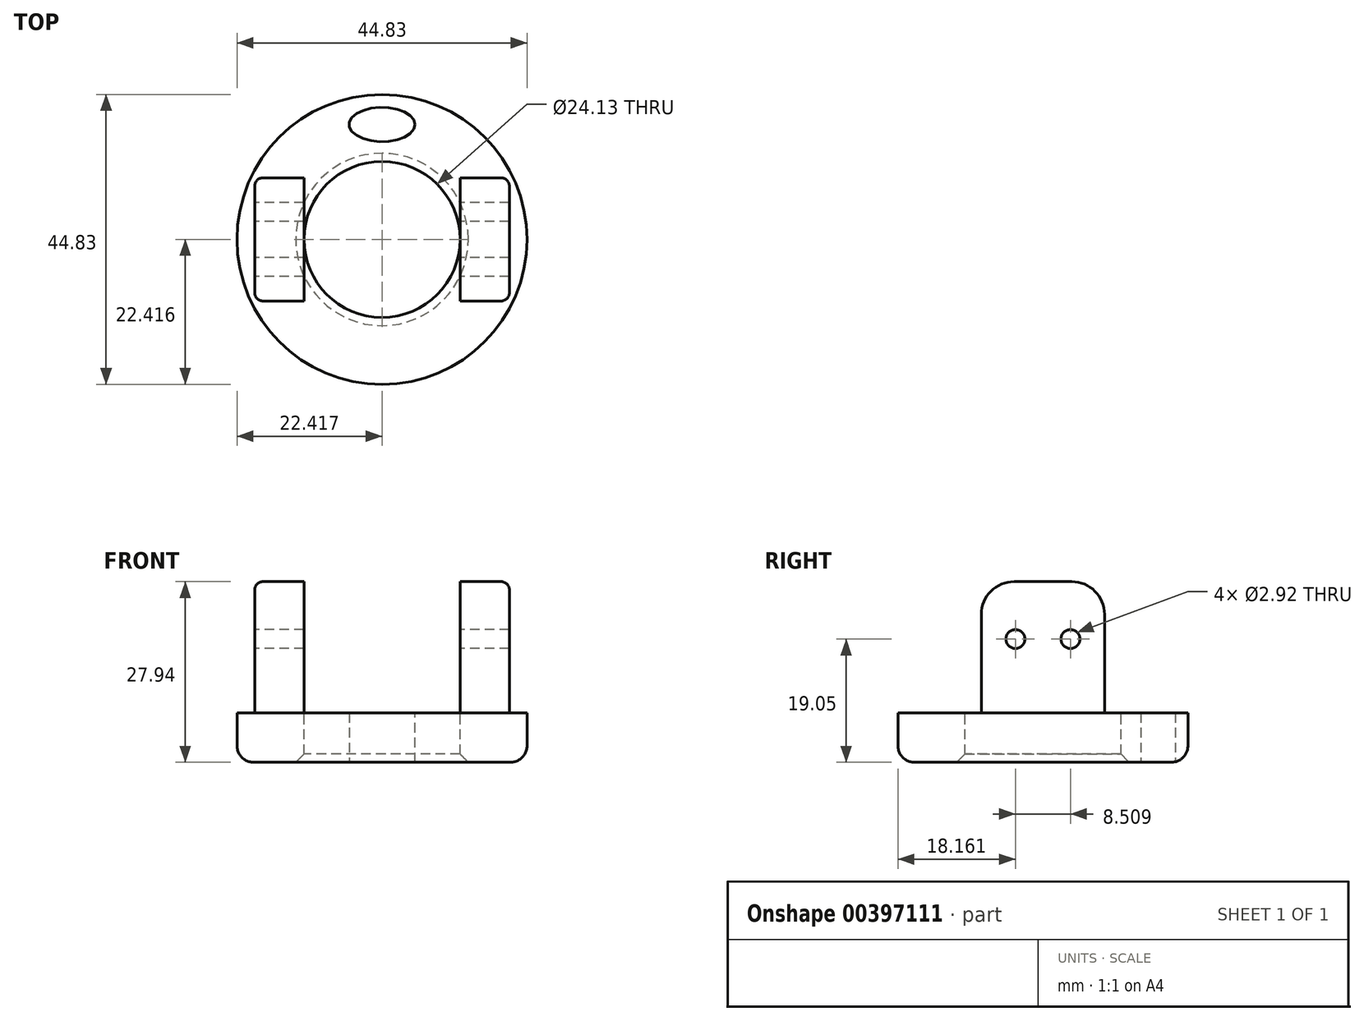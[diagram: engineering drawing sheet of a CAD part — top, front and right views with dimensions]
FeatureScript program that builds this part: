
annotation { "Feature Type Name" : "Feature", "Feature Type Description" : "" }
export const myFeature = defineFeature(function(context is Context, id is Id, definition is map)
    precondition{}
    {
        {
            var Q0;
            Q0=qCreatedBy(makeId("Top.planeOp"),FACE);
            var sketch = newSketch(context, id + "F0", { "sketchPlane" : qUnion([Q0])});
            skCircle(sketch, "E0", {"center": v(-27.57, -25.12) * mm, "radius": 22.42 * mm});
            skSolve(sketch);
        }
        {
            var Q0;
            Q0=makeQuery(id+"F0.imprint","IMPRINT",FACE,{"disambiguationData":[TD([[makeQuery(id+"F0.imprint","IMPRINT",EDGE,{"derivedFrom":sQuery(id+"F0.wireOp",EDGE,"E0")}),1.0]])]});
            extrude(context, id + "F1", {"entities" : qUnion([Q0]), "depth" : 7.62 * mm});
        }
        {
            var Q0;
            Q0=makeQuery(id+"F1.opExtrude","CAP_FACE",FACE,{"disambiguationData":[OSD([sQuery(id+"F0.wireOp",EDGE,"E0")])],"isStart":false});
            var sketch = newSketch(context, id + "F2", { "sketchPlane" : qUnion([Q0])});
            skCircle(sketch, "E1", {"center": v(-27.57, -25.12) * mm, "radius": 12.07 * mm});
            skEllipse(sketch, "E2", {"center": v(-27.57, -7.34) * mm, "majorRadius": 5.08 * mm, "minorRadius": 2.67 * mm, "majorAxis": v(1, 0)});
            skSolve(sketch);
        }
        {
            var Q0;
            Q0=makeQuery(id+"F2.imprint","IMPRINT",FACE,{"disambiguationData":[TD([[makeQuery(id+"F2.imprint","IMPRINT",EDGE,{"derivedFrom":sQuery(id+"F2.wireOp",EDGE,"E2")}),1.0]])]});
            var Q1;
            Q1=makeQuery(id+"F2.imprint","IMPRINT",FACE,{"disambiguationData":[TD([[makeQuery(id+"F2.imprint","IMPRINT",EDGE,{"derivedFrom":sQuery(id+"F2.wireOp",EDGE,"E1")}),1.0]])]});
            extrude(context, id + "F3", {"entities" : qUnion([Q0, Q1]), "operationType" : NewBodyOperationType.REMOVE, "oppositeDirection" : true, "depth" : 25.4 * mm});
        }
        {
            var Q0;
            Q0=makeQuery(id+"F1.opExtrude","CAP_FACE",FACE,{"disambiguationData":[OSD([sQuery(id+"F0.wireOp",EDGE,"E0")])],"isStart":false});
            var sketch = newSketch(context, id + "F4", { "sketchPlane" : qUnion([Q0])});
            skLineSegment(sketch, "E3.bottom", {"start": v(-7.89, -15.6) * mm, "end": v(-15.5, -15.6) * mm});
            skLineSegment(sketch, "E3.top", {"start": v(-7.89, -34.65) * mm, "end": v(-15.5, -34.65) * mm});
            skLineSegment(sketch, "E3.left", {"start": v(-7.89, -15.6) * mm, "end": v(-7.89, -34.65) * mm});
            skLineSegment(sketch, "E3.right", {"start": v(-15.5, -15.6) * mm, "end": v(-15.5, -34.65) * mm});
            skPoint(sketch, "E3.middle", {"position": v(-11.7, -25.12) * mm});
            skLineSegment(sketch, "E4.bottom", {"start": v(-39.64, -15.6) * mm, "end": v(-47.26, -15.6) * mm});
            skLineSegment(sketch, "E4.top", {"start": v(-39.64, -34.65) * mm, "end": v(-47.26, -34.65) * mm});
            skLineSegment(sketch, "E4.left", {"start": v(-39.64, -15.6) * mm, "end": v(-39.64, -34.65) * mm});
            skLineSegment(sketch, "E4.right", {"start": v(-47.26, -15.6) * mm, "end": v(-47.26, -34.65) * mm});
            skPoint(sketch, "E4.middle", {"position": v(-43.45, -25.12) * mm});
            skSolve(sketch);
        }
        {
            var Q0;
            Q0=makeQuery(id+"F4.imprint","IMPRINT",FACE,{"disambiguationData":[TD([[makeQuery(id+"F4.imprint","IMPRINT",EDGE,{"derivedFrom":sQuery(id+"F4.wireOp",EDGE,"E4.bottom")}),1.0]])]});
            var Q1;
            Q1=makeQuery(id+"F4.imprint","IMPRINT",FACE,{"disambiguationData":[TD([[makeQuery(id+"F4.imprint","IMPRINT",EDGE,{"derivedFrom":sQuery(id+"F4.wireOp",EDGE,"E3.bottom")}),1.0]])]});
            extrude(context, id + "F5", {"entities" : qUnion([Q0, Q1]), "operationType" : NewBodyOperationType.ADD, "depth" : 20.32 * mm});
        }
        {
            var Q0;
            Q0=makeQuery(id+"F5.opExtrude","CAP_EDGE",EDGE,{"disambiguationData":[OSD([sQuery(id+"F4.wireOp",EDGE,"E3.top")])],"isStart":false});
            var Q1;
            Q1=makeQuery(id+"F5.opExtrude","CAP_EDGE",EDGE,{"disambiguationData":[OSD([sQuery(id+"F4.wireOp",EDGE,"E3.bottom")])],"isStart":false});
            var Q2;
            Q2=makeQuery(id+"F5.opExtrude","CAP_EDGE",EDGE,{"disambiguationData":[OSD([sQuery(id+"F4.wireOp",EDGE,"E4.top")])],"isStart":false});
            var Q3;
            Q3=makeQuery(id+"F5.opExtrude","CAP_EDGE",EDGE,{"disambiguationData":[OSD([sQuery(id+"F4.wireOp",EDGE,"E4.bottom")])],"isStart":false});
            fillet(context, id + "F6", {"entities" : qUnion([Q0, Q1, Q2, Q3]), "radius" : 5.08 * mm, "tangentPropagation" : true, "allowEdgeOverflow" : false});
        }
        {
            var Q0;
            Q0=makeQuery(id+"F5.opExtrude","SWEPT_EDGE",EDGE,{"disambiguationData":[OSD([sQuery(id+"F4.wireOp",EDGE,"E3.top"),sQuery(id+"F4.wireOp",EDGE,"E3.left")])]});
            var Q1;
            Q1=makeQuery(id+"F5.opExtrude","SWEPT_EDGE",EDGE,{"disambiguationData":[OSD([sQuery(id+"F4.wireOp",EDGE,"E4.bottom"),sQuery(id+"F4.wireOp",EDGE,"E4.right")])]});
            fillet(context, id + "F7", {"entities" : qUnion([Q0, Q1]), "radius" : 1.27 * mm, "tangentPropagation" : true, "allowEdgeOverflow" : false});
        }
        {
            var Q0;
            Q0=makeQuery(id+"F5.opExtrude","SWEPT_FACE",FACE,{"disambiguationData":[OSD([sQuery(id+"F4.wireOp",EDGE,"E4.right")])]});
            var sketch = newSketch(context, id + "F8", { "sketchPlane" : qUnion([Q0])});
            skCircle(sketch, "E5", {"center": v(20.87, 19.05) * mm, "radius": 1.46 * mm});
            skCircle(sketch, "E6", {"center": v(29.38, 19.05) * mm, "radius": 1.46 * mm});
            skSolve(sketch);
        }
        {
            var Q0;
            Q0=makeQuery(id+"F8.imprint","IMPRINT",FACE,{"disambiguationData":[TD([[makeQuery(id+"F8.imprint","IMPRINT",EDGE,{"derivedFrom":sQuery(id+"F8.wireOp",EDGE,"E5")}),1.0]])]});
            var Q1;
            Q1=makeQuery(id+"F8.imprint","IMPRINT",FACE,{"disambiguationData":[TD([[makeQuery(id+"F8.imprint","IMPRINT",EDGE,{"derivedFrom":sQuery(id+"F8.wireOp",EDGE,"E6")}),1.0]])]});
            extrude(context, id + "F9", {"entities" : qUnion([Q0, Q1]), "operationType" : NewBodyOperationType.REMOVE, "oppositeDirection" : true, "depth" : 76.2 * mm});
        }
        {
            var Q0;
            Q0=makeQuery(id+"F1.opExtrude","CAP_EDGE",EDGE,{"disambiguationData":[OSD([sQuery(id+"F0.wireOp",EDGE,"E0")])],"isStart":true});
            fillet(context, id + "F10", {"entities" : qUnion([Q0]), "radius" : 2.54 * mm, "tangentPropagation" : true, "allowEdgeOverflow" : false});
        }
        {
            var Q0;
            Q0=makeQuery(id+"F3.boolean.opBoolean","INTERSECT",EDGE,{"derivedFrom":[makeQuery(id+"F1.opExtrude","CAP_FACE",FACE,{"disambiguationData":[OSD([sQuery(id+"F0.wireOp",EDGE,"E0")])],"isStart":true}),makeQuery(id+"F3.opExtrude","SWEPT_FACE",FACE,{"disambiguationData":[OSD([sQuery(id+"F2.wireOp",EDGE,"E1")])]})]});
            chamfer(context, id + "F11", {"entities" : qUnion([Q0]), "width" : 1.27 * mm, "tangentPropagation" : true});
        }
    });
